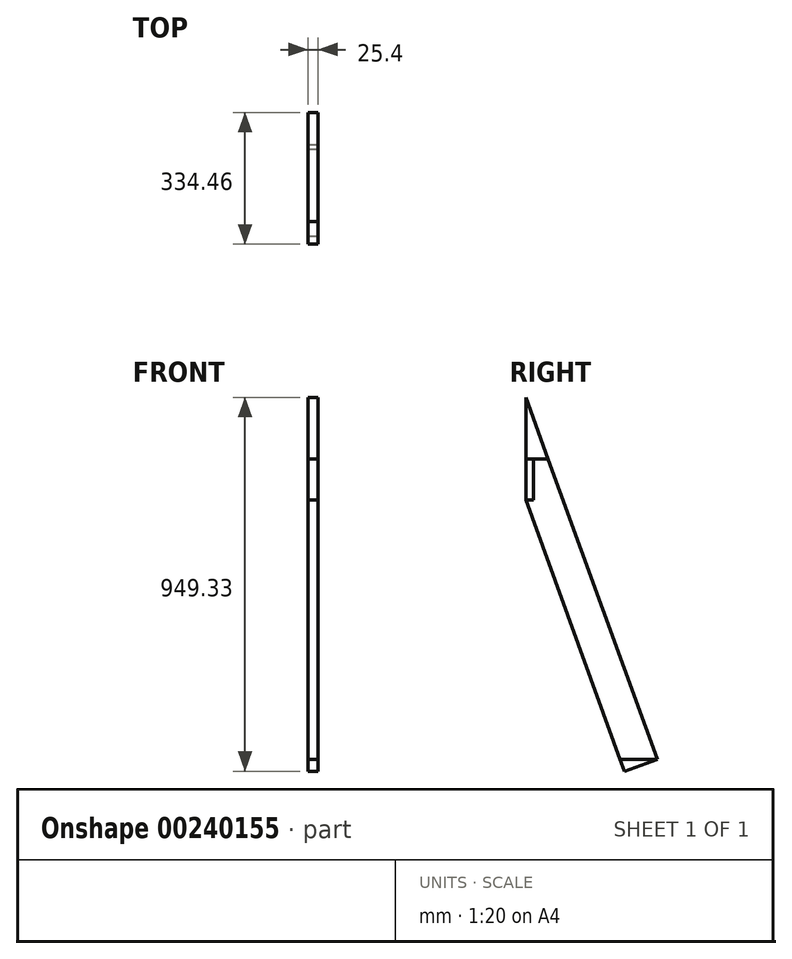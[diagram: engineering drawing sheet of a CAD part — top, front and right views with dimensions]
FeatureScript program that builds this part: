
annotation { "Feature Type Name" : "Feature", "Feature Type Description" : "" }
export const myFeature = defineFeature(function(context is Context, id is Id, definition is map)
    precondition{}
    {
        {
            var Q0;
            Q0=qCreatedBy(makeId("Right.planeOp"),FACE);
            var sketch = newSketch(context, id + "F0", { "sketchPlane" : qUnion([Q0])});
            skLineSegment(sketch, "E0.0", {"start": v(62.6, 81.46) * mm, "end": v(81.65, 81.46) * mm, "construction": true});
            skLineSegment(sketch, "E1.0", {"start": v(81.65, 81.46) * mm, "end": v(81.65, 184.65) * mm, "construction": true});
            skLineSegment(sketch, "E2", {"start": v(62.6, 81.46) * mm, "end": v(62.6, -580.53) * mm, "construction": true});
            skLineSegment(sketch, "E3", {"start": v(62.6, 81.46) * mm, "end": v(313.52, -607.94) * mm});
            skLineSegment(sketch, "E4", {"start": v(62.6, 81.46) * mm, "end": v(81.65, 81.46) * mm});
            skLineSegment(sketch, "E5", {"start": v(81.65, 81.46) * mm, "end": v(81.65, 184.65) * mm});
            skLineSegment(sketch, "E6", {"start": v(81.65, 184.65) * mm, "end": v(119.65, 184.65) * mm});
            skLineSegment(sketch, "E7", {"start": v(62.6, 184.65) * mm, "end": v(119.65, 184.65) * mm});
            skLineSegment(sketch, "E8", {"start": v(119.65, 184.65) * mm, "end": v(62.6, 341.39) * mm});
            skLineSegment(sketch, "E9", {"start": v(62.6, 81.46) * mm, "end": v(62.6, 341.39) * mm});
            skLineSegment(sketch, "E10", {"start": v(397.06, -577.54) * mm, "end": v(302.46, -577.54) * mm});
            skLineSegment(sketch, "E11", {"start": v(119.65, 184.65) * mm, "end": v(397.06, -577.54) * mm});
            skLineSegment(sketch, "E12", {"start": v(397.06, -577.54) * mm, "end": v(313.52, -607.94) * mm});
            skSolve(sketch);
        }
        {
            var Q0;
            {var subQ4=sQuery(id+"F0.wireOp",EDGE,"E8");Q0=makeQuery(id+"F0.imprint","IMPRINT",FACE,{"disambiguationData":[TD([[makeQuery(id+"F0.imprint","IMPRINT",EDGE,{"derivedFrom":subQ4}),1.0]])]});}
            extrude(context, id + "F1", {"entities" : qUnion([Q0]), "depth" : 25.4 * mm});
        }
        {
            var Q0;
            {var subQ3=sQuery(id+"F0.wireOp",EDGE,"E4");Q0=makeQuery(id+"F0.imprint","IMPRINT",FACE,{"disambiguationData":[TD([[makeQuery(id+"F0.imprint","IMPRINT",EDGE,{"derivedFrom":subQ3}),-1.0]])]});}
            extrude(context, id + "F2", {"entities" : qUnion([Q0]), "depth" : 25.4 * mm});
        }
        {
            var Q0;
            {var subQ0=sQuery(id+"F0.wireOp",EDGE,"E4");Q0=makeQuery(id+"F0.imprint","IMPRINT",FACE,{"disambiguationData":[TD([[makeQuery(id+"F0.imprint","IMPRINT",EDGE,{"derivedFrom":subQ0}),1.0]])]});}
            extrude(context, id + "F3", {"entities" : qUnion([Q0]), "depth" : 25.4 * mm});
        }
        {
            var Q0;
            {var subQ2=sQuery(id+"F0.wireOp",EDGE,"E10");Q0=makeQuery(id+"F0.imprint","IMPRINT",FACE,{"disambiguationData":[TD([[makeQuery(id+"F0.imprint","IMPRINT",EDGE,{"derivedFrom":subQ2}),1.0]])]});}
            extrude(context, id + "F4", {"entities" : qUnion([Q0]), "depth" : 25.4 * mm});
        }
    });
